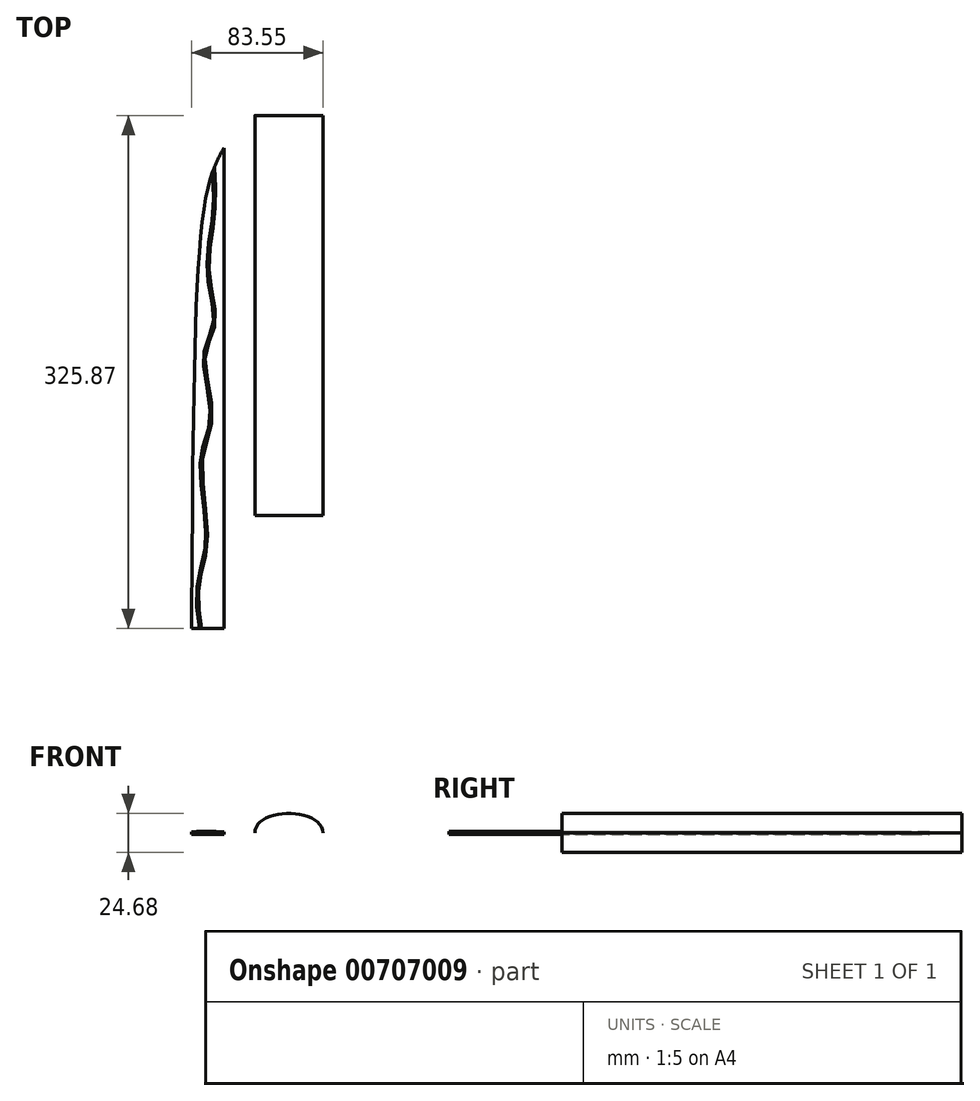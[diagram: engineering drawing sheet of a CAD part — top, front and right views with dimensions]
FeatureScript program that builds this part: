
annotation { "Feature Type Name" : "Feature", "Feature Type Description" : "" }
export const myFeature = defineFeature(function(context is Context, id is Id, definition is map)
    precondition{}
    {
        {
            var Q0;
            Q0=qCreatedBy(makeId("Front.planeOp"),FACE);
            var sketch = newSketch(context, id + "F0", { "sketchPlane" : qUnion([Q0])});
            skFitSpline(sketch, "E0", {"points": [v(-24.99, 0) * mm, v(18.2, 0) * mm], "startDerivative": vector(-0.54, 49.4) * mm, "endDerivative": vector(0.7, -49.3) * mm});
            skFitSpline(sketch, "E1.MirrorCS", {"points": [v(-24.99, 0) * mm, v(18.2, 0) * mm], "startDerivative": vector(-0.54, -49.4) * mm, "endDerivative": vector(0.7, 49.3) * mm});
            skSolve(sketch);
        }
        {
            var Q0;
            Q0=makeQuery(id+"F0.imprint","IMPRINT",FACE,{"disambiguationData":[TD([[makeQuery(id+"F0.imprint","IMPRINT",EDGE,{"derivedFrom":sQuery(id+"F0.wireOp",EDGE,"E0")}),-1.0]])]});
            extrude(context, id + "F1", {"entities" : qUnion([Q0]), "oppositeDirection" : true, "depth" : 254 * mm, "offsetDistance" : 25.4 * mm});
        }
        {
            var Q0;
            Q0=qCreatedBy(makeId("Top.planeOp"),FACE);
            var sketch = newSketch(context, id + "F2", { "sketchPlane" : qUnion([Q0])});
            skFitSpline(sketch, "E2", {"points": [v(-20.63, -71.87) * mm, v(-12.34, 196.88) * mm, v(0, 233.38) * mm], "startDerivative": vector(4.62, 464.1) * mm, "endDerivative": vector(59.81, 104.37) * mm});
            skLineSegment(sketch, "E3", {"start": v(0, 233.38) * mm, "end": v(0, -71.87) * mm});
            skLineSegment(sketch, "E4", {"start": v(0, -71.87) * mm, "end": v(-20.63, -71.87) * mm});
            skPoint(sketch, "E5.2.internal.snap0", {"position": v(-10.32, -71.87) * mm});
            skFitSpline(sketch, "E5", {"points": [v(-14.3, -71.87) * mm, v(-15.77, -44.44) * mm, v(-10.32, -15.38) * mm, v(-13.56, 35.75) * mm, v(-7.4, 62.9) * mm, v(-11.8, 101.5) * mm, v(-5.35, 122.5) * mm, v(-9.32, 153.77) * mm, v(-6.24, 188.06) * mm, v(-6.05, 221.14) * mm], "startDerivative": vector(-37.77, 274.45) * mm, "endDerivative": vector(-20.9, 292.34) * mm});
            skFitSpline(sketch, "E6.0", {"points": [v(-15.56, -72.04) * mm, v(-15.95, -69.18) * mm, v(-16.55, -64.88) * mm, v(-17.14, -59.16) * mm, v(-17.43, -54.9) * mm, v(-17.51, -50.67) * mm, v(-17.36, -47.2) * mm, v(-17.07, -44.45) * mm, v(-16.66, -41.73) * mm, v(-15.97, -38.4) * mm, v(-14.97, -34.42) * mm, v(-13.92, -30.38) * mm, v(-12.94, -26.2) * mm, v(-12.26, -22.52) * mm, v(-11.87, -19.42) * mm, v(-11.65, -17) * mm, v(-11.54, -14.49) * mm, v(-11.53, -11.85) * mm, v(-11.62, -9.12) * mm, v(-11.84, -5.35) * mm, v(-12.27, -0.46) * mm, v(-12.95, 5.58) * mm, v(-13.69, 11.69) * mm, v(-14.37, 17.75) * mm, v(-14.9, 23.66) * mm, v(-15.1, 28.37) * mm, v(-15.09, 31.97) * mm, v(-14.96, 34.56) * mm, v(-14.71, 37.04) * mm, v(-14.34, 39.4) * mm, v(-13.87, 41.63) * mm, v(-13.14, 44.48) * mm, v(-12.1, 47.83) * mm, v(-10.84, 51.67) * mm, v(-9.72, 55.46) * mm, v(-9.04, 58.7) * mm, v(-8.73, 61.42) * mm, v(-8.6, 64.26) * mm, v(-8.79, 68.12) * mm, v(-9.44, 73.1) * mm, v(-10.36, 78.28) * mm, v(-11.37, 83.56) * mm, v(-12.3, 88.81) * mm, v(-12.9, 93.07) * mm, v(-13.15, 96.35) * mm, v(-13.22, 98.74) * mm, v(-13.16, 100.66) * mm, v(-13.02, 102.14) * mm, v(-12.82, 103.59) * mm, v(-12.47, 105.31) * mm, v(-11.75, 107.93) * mm, v(-10.62, 110.97) * mm, v(-9.16, 114.36) * mm, v(-8.04, 117.1) * mm, v(-7.31, 119.3) * mm, v(-6.88, 120.99) * mm, v(-6.58, 122.7) * mm, v(-6.43, 124.5) * mm, v(-6.41, 126.41) * mm, v(-6.56, 129.06) * mm, v(-7, 132.56) * mm, v(-7.81, 137.02) * mm, v(-8.75, 141.65) * mm, v(-9.67, 146.42) * mm, v(-10.28, 150.45) * mm, v(-10.6, 153.7) * mm, v(-10.74, 156.13) * mm, v(-10.79, 158.55) * mm, v(-10.73, 161.76) * mm, v(-10.48, 165.74) * mm, v(-9.96, 170.47) * mm, v(-9.31, 175.16) * mm, v(-8.61, 179.81) * mm, v(-7.94, 184.44) * mm, v(-7.38, 189.03) * mm, v(-7, 193.61) * mm, v(-6.76, 198.2) * mm, v(-6.62, 204.31) * mm, v(-6.75, 211.94) * mm, v(-7.1, 218.02) * mm, v(-7.32, 221.05) * mm]});
            skSolve(sketch);
        }
        {
            var Q0;
            {var subQ0=sQuery(id+"F2.wireOp",EDGE,"E4");var subQ1=sQuery(id+"F2.wireOp",EDGE,"E2");var subQ2=makeQuery(id+"F2.imprint","INTERSECT",VERTEX,{"derivedFrom":[subQ1,subQ0]});Q0=makeQuery(id+"F2.imprint","IMPRINT",FACE,{"disambiguationData":[TD([[makeQuery(id+"F2.imprint","IMPRINT",EDGE,{"disambiguationData":[TD([[subQ2,-1.0]])],"derivedFrom":subQ1}),-1.0]])]});}
            var Q1;
            {var subQ0=sQuery(id+"F2.wireOp",EDGE,"E3");Q1=makeQuery(id+"F2.imprint","IMPRINT",FACE,{"disambiguationData":[TD([[makeQuery(id+"F2.imprint","IMPRINT",EDGE,{"derivedFrom":subQ0}),-1.0]])]});}
            extrude(context, id + "F3", {"entities" : qUnion([Q0, Q1]), "endBound" : BoundingType.SYMMETRIC, "oppositeDirection" : true, "depth" : 1.52 * mm, "offsetDistance" : 25.4 * mm});
        }
        {
            var Q0;
            {var subQ0=sQuery(id+"F2.wireOp",EDGE,"E5");Q0=makeQuery(id+"F2.imprint","IMPRINT",FACE,{"disambiguationData":[TD([[makeQuery(id+"F2.imprint","IMPRINT",EDGE,{"derivedFrom":subQ0}),1.0]])]});}
            extrude(context, id + "F4", {"entities" : qUnion([Q0]), "depth" : 0.88 * mm, "offsetDistance" : 25.4 * mm, "hasSecondDirection" : true, "secondDirectionOppositeDirection" : true, "secondDirectionDepth" : 0.76 * mm});
        }
        {
            var Q0;
            Q0=makeQuery(id+"F3.opExtrude","SWEPT_BODY",BODY,{"disambiguationData":[OSD([sQuery(id+"F2.wireOp",EDGE,"E2"),sQuery(id+"F2.wireOp",EDGE,"E4"),sQuery(id+"F2.wireOp",EDGE,"E6.0")])]});
            var Q1;
            Q1=makeQuery(id+"F3.opExtrude","SWEPT_BODY",BODY,{"disambiguationData":[OSD([sQuery(id+"F2.wireOp",EDGE,"E2"),sQuery(id+"F2.wireOp",EDGE,"E3"),sQuery(id+"F2.wireOp",EDGE,"E4"),sQuery(id+"F2.wireOp",EDGE,"E5")])]});
            var Q2;
            Q2=makeQuery(id+"F4.opExtrude","SWEPT_BODY",BODY,{"disambiguationData":[OSD([sQuery(id+"F2.wireOp",EDGE,"E2"),sQuery(id+"F2.wireOp",EDGE,"E4"),sQuery(id+"F2.wireOp",EDGE,"E5"),sQuery(id+"F2.wireOp",EDGE,"E6.0")])]});
            transform(context, id + "F5", {"entities" : qUnion([Q0, Q1, Q2]), "transformType" : TransformType.TRANSLATION_3D, "dx" : -44.7 * mm, "dy" : 0 * mm, "dz" : 0 * mm, "makeCopy" : false});
        }
    });
